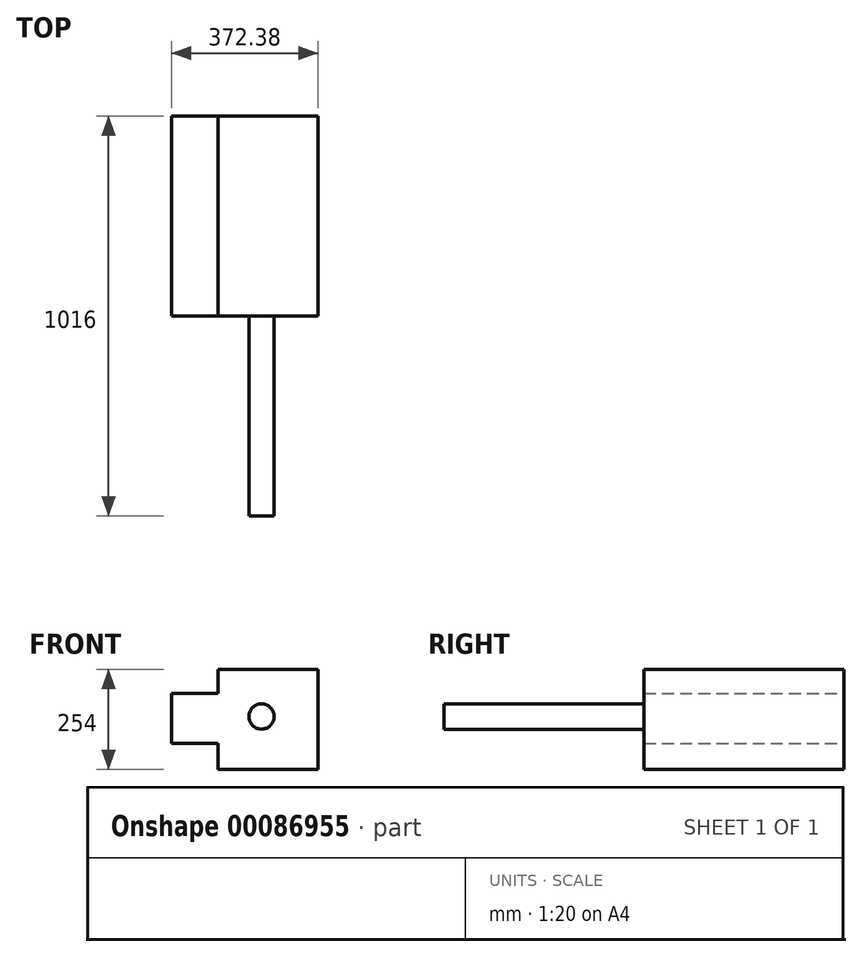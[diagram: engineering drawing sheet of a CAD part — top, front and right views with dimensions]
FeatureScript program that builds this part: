
annotation { "Feature Type Name" : "Feature", "Feature Type Description" : "" }
export const myFeature = defineFeature(function(context is Context, id is Id, definition is map)
    precondition{}
    {
        {
            var Q0;
            Q0=qCreatedBy(makeId("Front.planeOp"),FACE);
            var sketch = newSketch(context, id + "F0", { "sketchPlane" : qUnion([Q0])});
            skLineSegment(sketch, "E0.bottom", {"start": v(0, 0) * mm, "end": v(-254, 0) * mm});
            skLineSegment(sketch, "E0.top", {"start": v(0, 254) * mm, "end": v(-254, 254) * mm});
            skLineSegment(sketch, "E0.left", {"start": v(0, 0) * mm, "end": v(0, 254) * mm});
            skLineSegment(sketch, "E0.right", {"start": v(-254, 0) * mm, "end": v(-254, 254) * mm});
            skLineSegment(sketch, "E1.bottom", {"start": v(-254, 192.79) * mm, "end": v(-372.38, 192.79) * mm});
            skLineSegment(sketch, "E1.top", {"start": v(-254, 66.15) * mm, "end": v(-372.38, 66.15) * mm});
            skLineSegment(sketch, "E1.left", {"start": v(-254, 192.79) * mm, "end": v(-254, 66.15) * mm});
            skLineSegment(sketch, "E1.right", {"start": v(-372.38, 192.79) * mm, "end": v(-372.38, 66.15) * mm});
            skSolve(sketch);
        }
        {
            var Q0;
            {var subQ4=sQuery(id+"F0.wireOp",EDGE,"E0.bottom");Q0=makeQuery(id+"F0.imprint","IMPRINT",FACE,{"disambiguationData":[TD([[makeQuery(id+"F0.imprint","IMPRINT",EDGE,{"derivedFrom":subQ4}),-1.0]])]});}
            var Q1;
            {var subQ2=sQuery(id+"F0.wireOp",EDGE,"E1.bottom");Q1=makeQuery(id+"F0.imprint","IMPRINT",FACE,{"disambiguationData":[TD([[makeQuery(id+"F0.imprint","IMPRINT",EDGE,{"derivedFrom":subQ2}),1.0]])]});}
            extrude(context, id + "F1", {"entities" : qUnion([Q0, Q1]), "depth" : 508 * mm, "offsetDistance" : 25.4 * mm});
        }
        {
            var Q0;
            Q0=makeQuery(id+"F1.opExtrude","CAP_FACE",FACE,{"disambiguationData":[OSD([sQuery(id+"F0.wireOp",EDGE,"E0.bottom"),sQuery(id+"F0.wireOp",EDGE,"E0.top"),sQuery(id+"F0.wireOp",EDGE,"E0.left"),sQuery(id+"F0.wireOp",EDGE,"E0.right"),sQuery(id+"F0.wireOp",EDGE,"E1.bottom"),sQuery(id+"F0.wireOp",EDGE,"E1.top"),sQuery(id+"F0.wireOp",EDGE,"E1.right")])],"isStart":false});
            var sketch = newSketch(context, id + "F2", { "sketchPlane" : qUnion([Q0])});
            skCircle(sketch, "E2", {"center": v(-143.96, 134.36) * mm, "radius": 32.15 * mm});
            skSolve(sketch);
        }
        {
            var Q0;
            Q0=makeQuery(id+"F2.imprint","IMPRINT",FACE,{"disambiguationData":[TD([[makeQuery(id+"F2.imprint","IMPRINT",EDGE,{"derivedFrom":sQuery(id+"F2.wireOp",EDGE,"E2")}),1.0]])]});
            extrude(context, id + "F3", {"entities" : qUnion([Q0]), "operationType" : NewBodyOperationType.ADD, "depth" : -508 * mm, "offsetDistance" : 25.4 * mm});
        }
        {
            var Q0;
            Q0 = qSketchRegion(id + "F2", true);
            var Q1;
            Q1=makeQuery(id+"F1.opExtrude","CAP_FACE",FACE,{"disambiguationData":[OSD([sQuery(id+"F0.wireOp",EDGE,"E0.bottom"),sQuery(id+"F0.wireOp",EDGE,"E0.top"),sQuery(id+"F0.wireOp",EDGE,"E0.left"),sQuery(id+"F0.wireOp",EDGE,"E0.right"),sQuery(id+"F0.wireOp",EDGE,"E1.bottom"),sQuery(id+"F0.wireOp",EDGE,"E1.top"),sQuery(id+"F0.wireOp",EDGE,"E1.right")])],"isStart":false});
            extrude(context, id + "F4", {"entities" : qUnion([Q0, Q1]), "operationType" : NewBodyOperationType.ADD, "oppositeDirection" : true, "depth" : 508 * mm, "offsetDistance" : 25.4 * mm});
        }
        {
            var Q0;
            Q0 = qSketchRegion(id + "F2", true);
            extrude(context, id + "F5", {"entities" : qUnion([Q0]), "operationType" : NewBodyOperationType.ADD, "depth" : 508 * mm, "offsetDistance" : 25.4 * mm});
        }
    });
